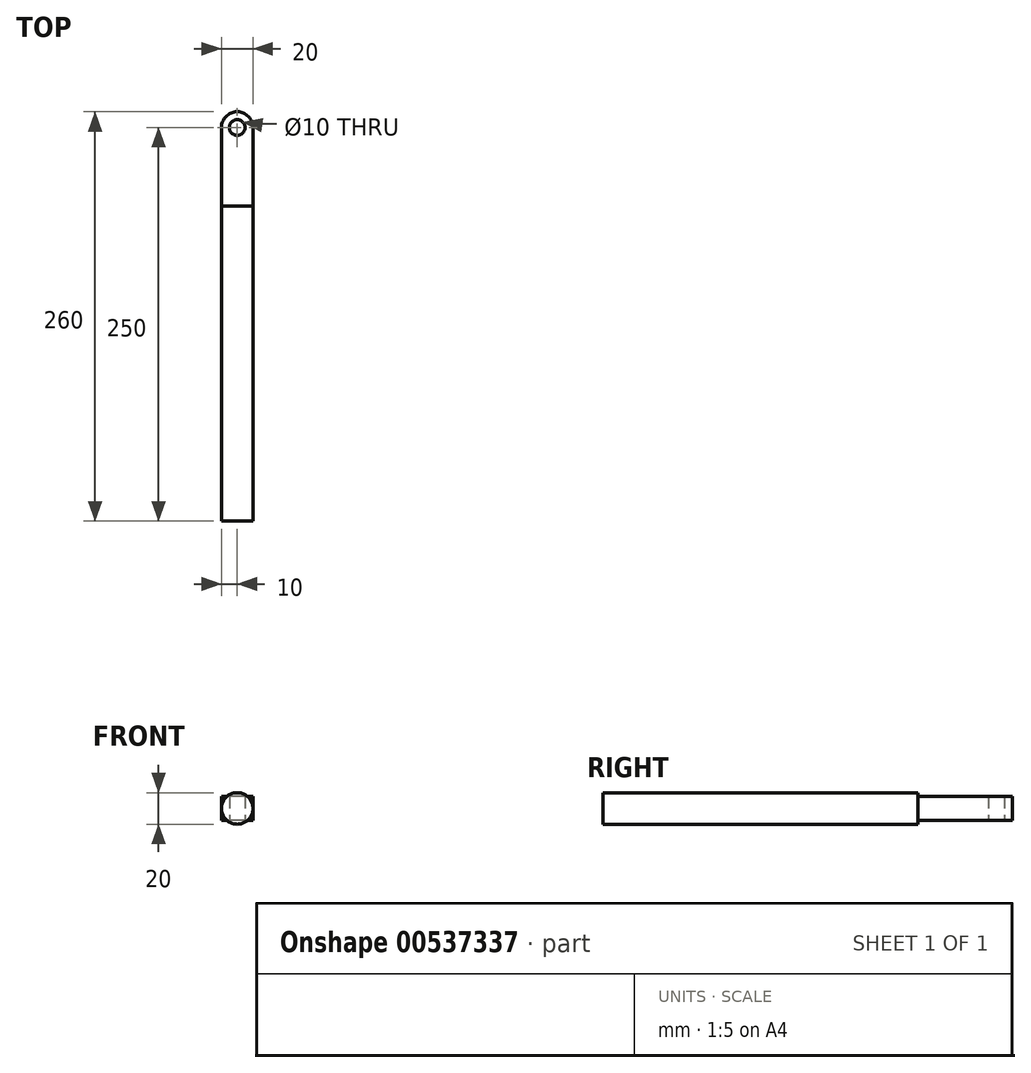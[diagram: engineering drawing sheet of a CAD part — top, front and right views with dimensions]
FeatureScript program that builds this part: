
annotation { "Feature Type Name" : "Feature", "Feature Type Description" : "" }
export const myFeature = defineFeature(function(context is Context, id is Id, definition is map)
    precondition{}
    {
        {
            var Q0;
            Q0=qCreatedBy(makeId("Top.planeOp"),FACE);
            var sketch = newSketch(context, id + "F0", { "sketchPlane" : qUnion([Q0])});
            skLineSegment(sketch, "E0.top", {"start": v(10, -25) * mm, "end": v(-10, -25) * mm});
            skLineSegment(sketch, "E0.left", {"start": v(10, 25) * mm, "end": v(10, -25) * mm});
            skLineSegment(sketch, "E0.right", {"start": v(-10, 25) * mm, "end": v(-10, -25) * mm});
            skPoint(sketch, "E0.middle", {"position": v(0, 0) * mm});
            skArc(sketch, "E1", {"start": v(10, 25) * mm, "mid": v(0, 35) * mm, "end": v(-10, 25) * mm});
            skCircle(sketch, "E2", {"center": v(0, 25) * mm, "radius": 5 * mm});
            skSolve(sketch);
        }
        {
            var Q0;
            Q0=makeQuery(id+"F0.imprint","IMPRINT",FACE,{"disambiguationData":[TD([[makeQuery(id+"F0.imprint","IMPRINT",EDGE,{"derivedFrom":sQuery(id+"F0.wireOp",EDGE,"E0.top")}),-1.0]])]});
            extrude(context, id + "F1", {"entities" : qUnion([Q0]), "endBound" : BoundingType.SYMMETRIC, "depth" : 15 * mm});
        }
        {
            var Q0;
            Q0=makeQuery(id+"F1.opExtrude","SWEPT_FACE",FACE,{"disambiguationData":[OSD([sQuery(id+"F0.wireOp",EDGE,"E0.top")])]});
            var sketch = newSketch(context, id + "F2", { "sketchPlane" : qUnion([Q0])});
            skCircle(sketch, "E3", {"center": v(0, 0) * mm, "radius": 10 * mm});
            skSolve(sketch);
        }
        {
            var Q0;
            Q0=qSketchRegion(id+"F2",true);
            extrude(context, id + "F3", {"entities" : qUnion([Q0]), "operationType" : NewBodyOperationType.ADD, "depth" : 200 * mm});
        }
    });
